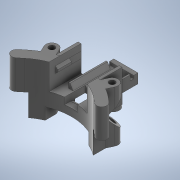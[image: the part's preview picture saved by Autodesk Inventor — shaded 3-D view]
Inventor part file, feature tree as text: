
AUTODESK INVENTOR PART (.ipt)
format: ipt  version: 2020 (Build 240168000, 168)  size: 792,576 bytes
history: native  units: mm
features: extrude x18, sketch x17, projected_geometry x15, other x5, chamfer x2, sweep x1, fillet x1
ambient origin geometry x8: Origin, YZ Plane, XZ Plane, XY Plane, X Axis, Y Axis, Z Axis, Center Point
bodies: Body1 (feature_tree)
feature tree (59):
  other  "Твердое тело1"
  extrude  "Выдавливание1"  Depth=35.0mm TaperAngle=0.0deg
  sketch  "Эскиз2"
  extrude  "Выдавливание2"  Depth=4.0mm
  sweep  "Сдвиг1"
  extrude  "Выдавливание5"  Depth=8.0mm
  extrude  "Выдавливание6"  Depth=35.0mm TaperAngle=0.0deg
  extrude  "Выдавливание7"  Depth=8.5mm
  extrude  "Выдавливание8"  TaperAngle=45.0deg  [1 undecoded]
  other  "РабПлоскость1"
  extrude  "Выдавливание9"  Depth=8.5mm
  extrude  "Выдавливание10"  TaperAngle=45.0deg  [1 undecoded]
  extrude  "Выдавливание11"  TaperAngle=0.0deg  [1 undecoded]
  sketch  "Эскиз13"
  other  "РабПлоскость2"
  sketch  "Эскиз14"
  extrude  "Выдавливание12"  Depth=5.0mm TaperAngle=0.0deg
  extrude  "Выдавливание13"  Depth=15.0mm TaperAngle=0.0deg
  other  "РабПлоскость3"
  extrude  "Выдавливание14"  Depth=15.0mm TaperAngle=0.0deg
  extrude  "Выдавливание15"  Depth=26.0mm
  extrude  "Выдавливание16"  Depth=6.0mm
  extrude  "Выдавливание17"  Depth=15.0mm TaperAngle=0.0deg
  chamfer  "Фаска1"  Distance=2.0mm
  other  "РабПлоскость4"
  sketch  "Эскиз18"
  extrude  "Выдавливание18"  Depth=1.5mm
  extrude  "Выдавливание19"  Depth=3.0mm
  extrude  "Выдавливание20"  Depth=6.0mm
  chamfer  "Фаска2"  Distance=2.5mm
  fillet  "Сопряжение1"  [1 undecoded]
  sketch  "Эскиз1"
  sketch  "Эскиз3"
  projected_geometry  "Спроецированная петля1"
  projected_geometry  "Спроецированная петля2"
  sketch  "3D эскиз1"
  sketch  "Эскиз4"
  sketch  "Эскиз6"
  projected_geometry  "Спроецированная петля4"
  sketch  "Эскиз7"
  projected_geometry  "Спроецированная петля5"
  sketch  "Эскиз9"
  projected_geometry  "Спроецированная петля7"
  sketch  "Эскиз11"
  projected_geometry  "Спроецированная петля8"
  sketch  "Эскиз12"
  projected_geometry  "Спроецированная петля9"
  projected_geometry  "Спроецированная петля10"
  sketch  "Эскиз15"
  sketch  "Эскиз16"
  projected_geometry  "Спроецированная петля11"
  projected_geometry  "Спроецированная петля12"
  sketch  "Эскиз17"
  projected_geometry  "Спроецированная петля13"
  projected_geometry  "Спроецированная петля14"
  projected_geometry  "Спроецированная петля15"
  projected_geometry  "Спроецированная петля16"
  sketch  "Эскиз19"
  projected_geometry  "Спроецированная петля17"
note: 4 required parameter values undecoded (feature->parameter linkage not recoverable at this tier; creation-order binding heuristic only, values carry confidence <= 0.55)
